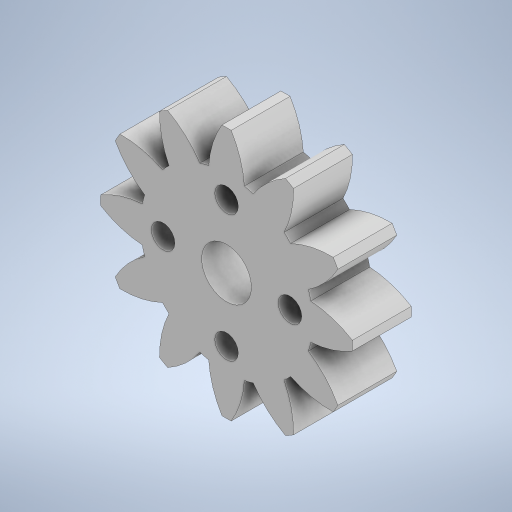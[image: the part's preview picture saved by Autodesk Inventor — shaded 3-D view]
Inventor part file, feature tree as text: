
AUTODESK INVENTOR PART (.ipt)
format: ipt  version: 2023.1 (Build 271208000, 208)  size: 343,552 bytes
history: native  units: mm
features: extrude x4, sketch x3, pattern_circular x1, projected_geometry x1
ambient origin geometry x8: Origin, YZ Plane, XZ Plane, XY Plane, X Axis, Y Axis, Z Axis, Center Point
bodies: Body1 (feature_tree)
feature tree (9):
  sketch  "스케치1"
  extrude  "돌출2"  Depth=24.0mm
  extrude  "돌출4"  Depth=28.0mm
  extrude  "돌출5"  Depth=19.0mm
  pattern_circular  "원형 패턴1"  [2 undecoded]
  extrude  "돌출6"  Depth=1.0mm
  sketch  "스케치2"
  projected_geometry  "투영된 루프1"
  sketch  "스케치3"
note: 2 required parameter values undecoded (feature->parameter linkage not recoverable at this tier; creation-order binding heuristic only, values carry confidence <= 0.55)
